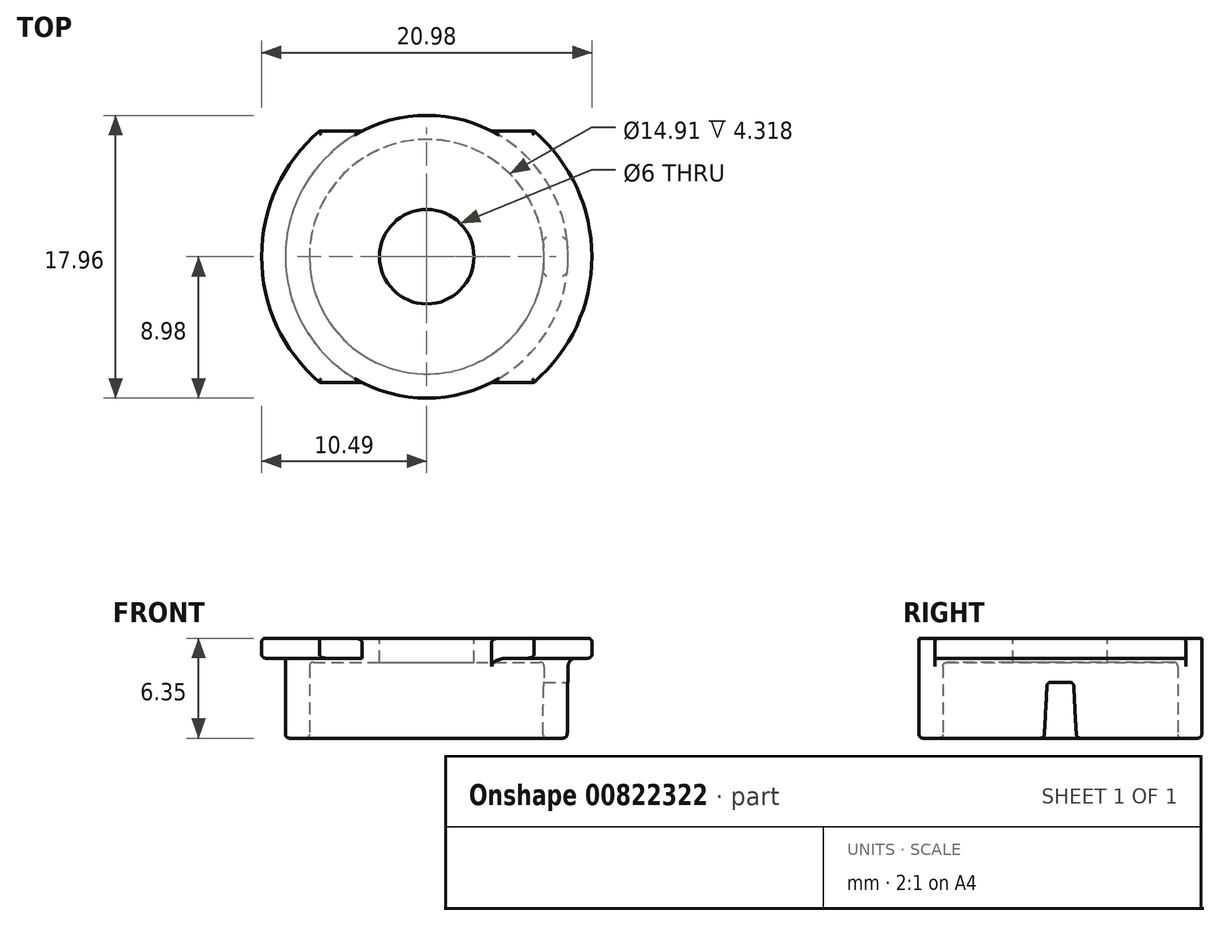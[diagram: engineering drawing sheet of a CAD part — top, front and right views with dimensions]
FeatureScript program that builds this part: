
annotation { "Feature Type Name" : "Feature", "Feature Type Description" : "" }
export const myFeature = defineFeature(function(context is Context, id is Id, definition is map)
    precondition{}
    {
        {
            var Q0;
            Q0=qCreatedBy(makeId("Top.planeOp"),FACE);
            var sketch = newSketch(context, id + "F0", { "sketchPlane" : qUnion([Q0])});
            skCircle(sketch, "E0", {"center": v(0, 0) * mm, "radius": 10.5 * mm});
            skLineSegment(sketch, "E1", {"start": v(-6.81, 7.98) * mm, "end": v(6.81, 7.98) * mm});
            skLineSegment(sketch, "E2", {"start": v(-6.81, -7.98) * mm, "end": v(6.81, -7.98) * mm});
            skSolve(sketch);
        }
        {
            var Q0;
            {var subQ0=sQuery(id+"F0.wireOp",EDGE,"E1");Q0=makeQuery(id+"F0.imprint","IMPRINT",FACE,{"disambiguationData":[TD([[makeQuery(id+"F0.imprint","IMPRINT",EDGE,{"derivedFrom":subQ0}),-1.0]])]});}
            extrude(context, id + "F1", {"entities" : qUnion([Q0]), "depth" : 1.27 * mm, "offsetDistance" : 25.4 * mm});
        }
        {
            var Q0;
            Q0=makeQuery(id+"F1.opExtrude","CAP_FACE",FACE,{"disambiguationData":[OSD([sQuery(id+"F0.wireOp",EDGE,"E0"),sQuery(id+"F0.wireOp",EDGE,"E1"),sQuery(id+"F0.wireOp",EDGE,"E2")])],"isStart":true});
            var sketch = newSketch(context, id + "F2", { "sketchPlane" : qUnion([Q0])});
            skCircle(sketch, "E3", {"center": v(0, 0) * mm, "radius": 8.98 * mm});
            skSolve(sketch);
        }
        {
            var Q0;
            Q0 = qSketchRegion(id + "F2", true);
            var Q1;
            Q1=makeQuery(id+"F1.opExtrude","CAP_FACE",FACE,{"disambiguationData":[OSD([sQuery(id+"F0.wireOp",EDGE,"E0"),sQuery(id+"F0.wireOp",EDGE,"E1"),sQuery(id+"F0.wireOp",EDGE,"E2")])],"isStart":false});
            extrude(context, id + "F3", {"entities" : qUnion([Q0]), "operationType" : NewBodyOperationType.ADD, "endBound" : BoundingType.UP_TO_SURFACE, "oppositeDirection" : true, "depth" : 5.08 * mm, "endBoundEntityFace" : qUnion([Q1]), "offsetDistance" : 25.4 * mm});
        }
        {
            var Q0;
            Q0=makeQuery(id+"F3.boolean.opBoolean","MERGE",FACE,{"derivedFrom":[makeQuery(id+"F1.opExtrude","CAP_FACE",FACE,{"disambiguationData":[OSD([sQuery(id+"F0.wireOp",EDGE,"E0"),sQuery(id+"F0.wireOp",EDGE,"E1"),sQuery(id+"F0.wireOp",EDGE,"E2")])],"isStart":true}),makeQuery(id+"F3.opExtrude","CAP_FACE",FACE,{"disambiguationData":[OSD([sQuery(id+"F2.wireOp",EDGE,"E3")])],"isStart":true})]});
            var sketch = newSketch(context, id + "F4", { "sketchPlane" : qUnion([Q0])});
            skCircle(sketch, "E4", {"center": v(0, 0) * mm, "radius": 8.98 * mm});
            skSolve(sketch);
        }
        {
            var Q0;
            Q0 = qSketchRegion(id + "F4", true);
            extrude(context, id + "F5", {"entities" : qUnion([Q0]), "operationType" : NewBodyOperationType.ADD, "depth" : 5.08 * mm, "offsetDistance" : 25.4 * mm});
        }
        {
            var Q0;
            Q0=makeQuery(id+"F5.opExtrude","CAP_FACE",FACE,{"disambiguationData":[OSD([sQuery(id+"F4.wireOp",EDGE,"E4")])],"isStart":false});
            var sketch = newSketch(context, id + "F6", { "sketchPlane" : qUnion([Q0])});
            skCircle(sketch, "E5", {"center": v(0, 0) * mm, "radius": 7.45 * mm});
            skSolve(sketch);
        }
        {
            var Q0;
            Q0 = qSketchRegion(id + "F6", true);
            extrude(context, id + "F7", {"entities" : qUnion([Q0]), "operationType" : NewBodyOperationType.REMOVE, "oppositeDirection" : true, "depth" : 4.83 * mm, "offsetDistance" : 25.4 * mm});
        }
        {
            var Q0;
            {var subQ0=sQuery(id+"F0.wireOp",EDGE,"E2");var subQ1=sQuery(id+"F0.wireOp",EDGE,"E1");var subQ2=sQuery(id+"F0.wireOp",EDGE,"E0");Q0=makeQuery(id+"F3.boolean.opBoolean","MERGE",FACE,{"derivedFrom":[makeQuery(id+"F1.opExtrude","CAP_FACE",FACE,{"disambiguationData":[OSD([subQ2,subQ1,subQ0])],"isStart":false}),makeQuery(id+"F3.opExtrude","CAP_FACE",FACE,{"disambiguationData":[OSD([subQ2,subQ1,subQ0])],"isStart":false})]});}
            var sketch = newSketch(context, id + "F8", { "sketchPlane" : qUnion([Q0])});
            skCircle(sketch, "E6", {"center": v(0, 0) * mm, "radius": 3 * mm});
            skSolve(sketch);
        }
        {
            var Q0;
            Q0 = qSketchRegion(id + "F8", true);
            extrude(context, id + "F9", {"entities" : qUnion([Q0]), "operationType" : NewBodyOperationType.REMOVE, "endBound" : BoundingType.UP_TO_NEXT, "oppositeDirection" : true, "depth" : 25.4 * mm, "offsetDistance" : 25.4 * mm});
        }
        {
            var Q0;
            Q0=qCreatedBy(makeId("Top.planeOp"),FACE);
            cPlane(context, id + "F10", {"entities" : qUnion([Q0]), "cplaneType" : CPlaneType.OFFSET, "offset" : 1.52 * mm, "oppositeDirection" : true, "width" : 152.4 * mm, "height" : 152.4 * mm});
        }
        {
            var Q0;
            Q0=qCreatedBy(id+"F10.planeOp",FACE);
            var sketch = newSketch(context, id + "F11", { "sketchPlane" : qUnion([Q0])});
            skLineSegment(sketch, "E7", {"start": v(8.94, 0.84) * mm, "end": v(7.4, 0.84) * mm});
            skLineSegment(sketch, "E8", {"start": v(8.94, -0.84) * mm, "end": v(7.4, -0.84) * mm});
            skArc(sketch, "E9", {"start": v(7.4, 0.84) * mm, "mid": v(7.45, 0) * mm, "end": v(7.4, -0.84) * mm});
            skArc(sketch, "E10", {"start": v(8.94, 0.84) * mm, "mid": v(8.98, 0) * mm, "end": v(8.94, -0.84) * mm});
            skSolve(sketch);
        }
        {
            var Q0;
            Q0 = qSketchRegion(id + "F11", true);
            extrude(context, id + "F12", {"entities" : qUnion([Q0]), "operationType" : NewBodyOperationType.REMOVE, "endBound" : BoundingType.UP_TO_NEXT, "oppositeDirection" : true, "depth" : 25.4 * mm, "offsetDistance" : 25.4 * mm, "hasDraft" : true, "draftAngle" : 3 * degree});
        }
        {
            var Q0;
            Q0=makeQuery(id+"F7.boolean.opBoolean","COPY",EDGE,{"derivedFrom":makeQuery(id+"F7.opExtrude","CAP_EDGE",EDGE,{"disambiguationData":[OSD([sQuery(id+"F6.wireOp",EDGE,"E5")])],"isStart":false})});
            fillet(context, id + "F13", {"entities" : qUnion([Q0]), "radius" : 0.25 * mm, "tangentPropagation" : true, "allowEdgeOverflow" : false});
        }
        {
            var Q0;
            Q0=makeQuery(id+"F12.boolean.opBoolean","COPY",EDGE,{"derivedFrom":makeQuery(id+"F12.opExtrude","CAP_EDGE",EDGE,{"disambiguationData":[OSD([sQuery(id+"F11.wireOp",EDGE,"E10")])],"isStart":true})});
            var Q1;
            Q1=makeQuery(id+"F12.boolean.opBoolean","COPY",EDGE,{"derivedFrom":makeQuery(id+"F12.opExtrude","CAP_EDGE",EDGE,{"disambiguationData":[OSD([sQuery(id+"F11.wireOp",EDGE,"E9")])],"isStart":true})});
            var Q2;
            Q2=makeQuery(id+"F12.boolean.opBoolean","COPY",EDGE,{"derivedFrom":makeQuery(id+"F12.opExtrude","CAP_EDGE",EDGE,{"disambiguationData":[OSD([sQuery(id+"F11.wireOp",EDGE,"E7")])],"isStart":true})});
            var Q3;
            Q3=makeQuery(id+"F12.boolean.opBoolean","COPY",EDGE,{"derivedFrom":makeQuery(id+"F12.opExtrude","CAP_EDGE",EDGE,{"disambiguationData":[OSD([sQuery(id+"F11.wireOp",EDGE,"E8")])],"isStart":true})});
            var Q4;
            Q4=makeQuery(id+"F12.boolean.opBoolean","COPY",EDGE,{"derivedFrom":makeQuery(id+"F12.opExtrude","TWEAK_EDGE",EDGE,{"derivedFrom":[makeQuery(id+"F5.opExtrude","CAP_FACE",FACE,{"disambiguationData":[OSD([sQuery(id+"F4.wireOp",EDGE,"E4")])],"isStart":false}),makeQuery(id+"F11.imprint","IMPRINT",EDGE,{"derivedFrom":sQuery(id+"F11.wireOp",EDGE,"E8")})]})});
            var Q5;
            Q5=makeQuery(id+"F12.boolean.opBoolean","COPY",EDGE,{"derivedFrom":makeQuery(id+"F12.opExtrude","TWEAK_EDGE",EDGE,{"derivedFrom":[makeQuery(id+"F5.opExtrude","CAP_FACE",FACE,{"disambiguationData":[OSD([sQuery(id+"F4.wireOp",EDGE,"E4")])],"isStart":false}),makeQuery(id+"F11.imprint","IMPRINT",EDGE,{"derivedFrom":sQuery(id+"F11.wireOp",EDGE,"E7")})]})});
            fillet(context, id + "F14", {"entities" : qUnion([Q0, Q1, Q2, Q3, Q4, Q5]), "radius" : 0.25 * mm, "tangentPropagation" : true, "allowEdgeOverflow" : false});
        }
        {
            var Q0;
            Q0=qCreatedBy(makeId("Front.planeOp"),FACE);
            var sketch = newSketch(context, id + "F15", { "sketchPlane" : qUnion([Q0])});
            skLineSegment(sketch, "E11", {"start": v(0, 0) * mm, "end": v(0, -25.4) * mm, "construction": true});
            skSolve(sketch);
        }
        {
            var Q0;
            {var subQ1=sQuery(id+"F4.wireOp",EDGE,"E4");Q0=makeQuery(id+"FYQlqfAHaxeDl4F_1.1.F12.boolean.opBoolean","SPLIT",FACE,{"disambiguationData":[TD([makeQuery(id+"FYQlqfAHaxeDl4F_1.1.F12.opExtrude","SWEPT_FACE",FACE,{"disambiguationData":[OSD([sQuery(id+"F11.wireOp",EDGE,"E7")])]})])],"derivedFrom":makeQuery(id+"F5.opExtrude","CAP_FACE",FACE,{"disambiguationData":[OSD([subQ1])],"isStart":false})});}
            var Q1;
            {var subQ0=sQuery(id+"F11.wireOp",EDGE,"E8");var subQ1=sQuery(id+"F4.wireOp",EDGE,"E4");var subQ4=sQuery(id+"F11.wireOp",EDGE,"E7");Q1=makeQuery(id+"FYQlqfAHaxeDl4F_1.3.F12.boolean.opBoolean","SPLIT",FACE,{"disambiguationData":[TD([makeQuery(id+"FYQlqfAHaxeDl4F_1.3.F12.opExtrude","SWEPT_FACE",FACE,{"disambiguationData":[OSD([subQ4])]})])],"derivedFrom":makeQuery(id+"FYQlqfAHaxeDl4F_1.2.F12.boolean.opBoolean","SPLIT",FACE,{"disambiguationData":[TD([makeQuery(id+"FYQlqfAHaxeDl4F_1.2.F12.opExtrude","SWEPT_FACE",FACE,{"disambiguationData":[OSD([subQ0])]})])],"derivedFrom":makeQuery(id+"FYQlqfAHaxeDl4F_1.1.F12.boolean.opBoolean","SPLIT",FACE,{"disambiguationData":[TD([makeQuery(id+"FYQlqfAHaxeDl4F_1.1.F12.opExtrude","SWEPT_FACE",FACE,{"disambiguationData":[OSD([subQ0])]})])],"derivedFrom":makeQuery(id+"F5.opExtrude","CAP_FACE",FACE,{"disambiguationData":[OSD([subQ1])],"isStart":false})})})});}
            var Q2;
            {var subQ1=sQuery(id+"F4.wireOp",EDGE,"E4");var subQ8=sQuery(id+"F11.wireOp",EDGE,"E8");Q2=makeQuery(id+"FYQlqfAHaxeDl4F_1.3.F12.boolean.opBoolean","SPLIT",FACE,{"disambiguationData":[TD([makeQuery(id+"FYQlqfAHaxeDl4F_1.3.F12.opExtrude","SWEPT_FACE",FACE,{"disambiguationData":[OSD([subQ8])]})])],"derivedFrom":makeQuery(id+"FYQlqfAHaxeDl4F_1.2.F12.boolean.opBoolean","SPLIT",FACE,{"disambiguationData":[TD([makeQuery(id+"FYQlqfAHaxeDl4F_1.2.F12.opExtrude","SWEPT_FACE",FACE,{"disambiguationData":[OSD([subQ8])]})])],"derivedFrom":makeQuery(id+"FYQlqfAHaxeDl4F_1.1.F12.boolean.opBoolean","SPLIT",FACE,{"disambiguationData":[TD([makeQuery(id+"FYQlqfAHaxeDl4F_1.1.F12.opExtrude","SWEPT_FACE",FACE,{"disambiguationData":[OSD([subQ8])]})])],"derivedFrom":makeQuery(id+"F5.opExtrude","CAP_FACE",FACE,{"disambiguationData":[OSD([subQ1])],"isStart":false})})})});}
            var Q3;
            {var subQ0=sQuery(id+"F11.wireOp",EDGE,"E8");var subQ1=sQuery(id+"F4.wireOp",EDGE,"E4");var subQ3=sQuery(id+"F11.wireOp",EDGE,"E7");Q3=makeQuery(id+"FYQlqfAHaxeDl4F_1.2.F12.boolean.opBoolean","SPLIT",FACE,{"disambiguationData":[TD([makeQuery(id+"FYQlqfAHaxeDl4F_1.2.F12.opExtrude","SWEPT_FACE",FACE,{"disambiguationData":[OSD([subQ3])]})])],"derivedFrom":makeQuery(id+"FYQlqfAHaxeDl4F_1.1.F12.boolean.opBoolean","SPLIT",FACE,{"disambiguationData":[TD([makeQuery(id+"FYQlqfAHaxeDl4F_1.1.F12.opExtrude","SWEPT_FACE",FACE,{"disambiguationData":[OSD([subQ0])]})])],"derivedFrom":makeQuery(id+"F5.opExtrude","CAP_FACE",FACE,{"disambiguationData":[OSD([subQ1])],"isStart":false})})});}
            fillet(context, id + "F16", {"entities" : qUnion([Q0, Q1, Q2, Q3]), "radius" : 0.25 * mm, "tangentPropagation" : true, "allowEdgeOverflow" : false});
        }
        {
            var Q0;
            Q0=makeQuery(id+"F5.boolean.opBoolean","SPLIT",EDGE,{"disambiguationData":[OD(1.0)],"derivedFrom":makeQuery(id+"F5.opExtrude","CAP_EDGE",EDGE,{"disambiguationData":[OSD([sQuery(id+"F4.wireOp",EDGE,"E4")])],"isStart":true})});
            var Q1;
            Q1=makeQuery(id+"F5.boolean.opBoolean","SPLIT",EDGE,{"disambiguationData":[OD(0.0)],"derivedFrom":makeQuery(id+"F5.opExtrude","CAP_EDGE",EDGE,{"disambiguationData":[OSD([sQuery(id+"F4.wireOp",EDGE,"E4")])],"isStart":true})});
            fillet(context, id + "F17", {"entities" : qUnion([Q0, Q1]), "radius" : 0.5 * mm, "tangentPropagation" : true, "allowEdgeOverflow" : false});
        }
        {
            var Q0;
            {var subQ1=sQuery(id+"F0.wireOp",EDGE,"E1");var subQ2=sQuery(id+"F0.wireOp",EDGE,"E0");Q0=makeQuery(id+"F3.boolean.opBoolean","SPLIT",EDGE,{"disambiguationData":[TD([makeQuery(id+"F1.opExtrude","SWEPT_FACE",FACE,{"disambiguationData":[OSD([subQ2]),TDD([makeQuery(id+"F0.imprint","IMPRINT",EDGE,{"disambiguationData":[TD([[makeQuery(id+"F0.imprint","INTERSECT",VERTEX,{"disambiguationData":[OD(0.0)],"derivedFrom":[subQ2,subQ1]}),-1.0]])],"derivedFrom":subQ2})])]})])],"derivedFrom":makeQuery(id+"F1.opExtrude","CAP_EDGE",EDGE,{"disambiguationData":[OSD([subQ1])],"isStart":false})});}
            var Q1;
            {var subQ0=sQuery(id+"F0.wireOp",EDGE,"E2");var subQ1=sQuery(id+"F0.wireOp",EDGE,"E1");var subQ2=sQuery(id+"F0.wireOp",EDGE,"E0");var subQ3=makeQuery(id+"F1.opExtrude","CAP_FACE",FACE,{"disambiguationData":[OSD([subQ2,subQ1,subQ0])],"isStart":false});var subQ4=sQuery(id+"F2.wireOp",EDGE,"E3");var subQ5=makeQuery(id+"F1.opExtrude","CAP_EDGE",EDGE,{"disambiguationData":[OSD([subQ0])],"isStart":true});var subQ6=makeQuery(id+"F2.imprint","INTERSECT",VERTEX,{"disambiguationData":[OD(1.0)],"derivedFrom":[subQ5,subQ4]});var subQ7=makeQuery(id+"F1.opExtrude","CAP_EDGE",EDGE,{"disambiguationData":[OSD([subQ1])],"isStart":true});var subQ9=makeQuery(id+"F2.imprint","INTERSECT",VERTEX,{"disambiguationData":[OD(0.0)],"derivedFrom":[subQ7,subQ4]});var subQ10=makeQuery(id+"F2.imprint","INTERSECT",VERTEX,{"disambiguationData":[OD(0.0)],"derivedFrom":[subQ5,subQ4]});Q1=makeQuery(id+"F3.boolean.opBoolean","SPLIT",EDGE,{"disambiguationData":[TD([makeQuery(id+"F1.opExtrude","SWEPT_FACE",FACE,{"disambiguationData":[OSD([subQ1])]})])],"derivedFrom":makeQuery(id+"F3.opExtrude","TWEAK_EDGE",EDGE,{"derivedFrom":[subQ3,makeQuery(id+"F2.imprint","IMPRINT",EDGE,{"disambiguationData":[TD([[subQ10,1.0]])],"derivedFrom":subQ4}),makeQuery(id+"F2.imprint","IMPRINT",EDGE,{"disambiguationData":[TD([[subQ10,-1.0]])],"derivedFrom":subQ4}),makeQuery(id+"F2.imprint","IMPRINT",EDGE,{"disambiguationData":[TD([[subQ9,-1.0]])],"derivedFrom":subQ4}),makeQuery(id+"F2.imprint","IMPRINT",EDGE,{"disambiguationData":[TD([[subQ6,1.0]])],"derivedFrom":subQ4})]})});}
            var Q2;
            {var subQ0=sQuery(id+"F0.wireOp",EDGE,"E1");var subQ2=sQuery(id+"F0.wireOp",EDGE,"E0");Q2=makeQuery(id+"F3.boolean.opBoolean","SPLIT",EDGE,{"disambiguationData":[TD([makeQuery(id+"F1.opExtrude","SWEPT_FACE",FACE,{"disambiguationData":[OSD([subQ2]),TDD([makeQuery(id+"F0.imprint","IMPRINT",EDGE,{"disambiguationData":[TD([[makeQuery(id+"F0.imprint","INTERSECT",VERTEX,{"disambiguationData":[OD(1.0)],"derivedFrom":[subQ2,subQ0]}),1.0]])],"derivedFrom":subQ2})])]})])],"derivedFrom":makeQuery(id+"F1.opExtrude","CAP_EDGE",EDGE,{"disambiguationData":[OSD([subQ0])],"isStart":false})});}
            var Q3;
            {var subQ0=sQuery(id+"F0.wireOp",EDGE,"E0");Q3=makeQuery(id+"F1.opExtrude","CAP_EDGE",EDGE,{"disambiguationData":[OSD([subQ0]),TDD([makeQuery(id+"F0.imprint","IMPRINT",EDGE,{"disambiguationData":[TD([[makeQuery(id+"F0.imprint","INTERSECT",VERTEX,{"disambiguationData":[OD(1.0)],"derivedFrom":[subQ0,sQuery(id+"F0.wireOp",EDGE,"E1")]}),1.0]])],"derivedFrom":subQ0})])],"isStart":false});}
            var Q4;
            {var subQ0=sQuery(id+"F0.wireOp",EDGE,"E2");var subQ1=sQuery(id+"F0.wireOp",EDGE,"E1");var subQ2=sQuery(id+"F0.wireOp",EDGE,"E0");Q4=makeQuery(id+"F3.boolean.opBoolean","SPLIT",EDGE,{"disambiguationData":[TD([makeQuery(id+"F1.opExtrude","SWEPT_FACE",FACE,{"disambiguationData":[OSD([subQ2]),TDD([makeQuery(id+"F0.imprint","IMPRINT",EDGE,{"disambiguationData":[TD([[makeQuery(id+"F0.imprint","INTERSECT",VERTEX,{"disambiguationData":[OD(1.0)],"derivedFrom":[subQ2,subQ1]}),1.0]])],"derivedFrom":subQ2})])]})])],"derivedFrom":makeQuery(id+"F1.opExtrude","CAP_EDGE",EDGE,{"disambiguationData":[OSD([subQ0])],"isStart":false})});}
            var Q5;
            {var subQ0=sQuery(id+"F0.wireOp",EDGE,"E2");var subQ1=sQuery(id+"F0.wireOp",EDGE,"E1");var subQ2=sQuery(id+"F0.wireOp",EDGE,"E0");var subQ3=makeQuery(id+"F1.opExtrude","CAP_FACE",FACE,{"disambiguationData":[OSD([subQ2,subQ1,subQ0])],"isStart":false});var subQ4=sQuery(id+"F2.wireOp",EDGE,"E3");var subQ5=makeQuery(id+"F1.opExtrude","CAP_EDGE",EDGE,{"disambiguationData":[OSD([subQ0])],"isStart":true});var subQ6=makeQuery(id+"F2.imprint","INTERSECT",VERTEX,{"disambiguationData":[OD(1.0)],"derivedFrom":[subQ5,subQ4]});var subQ7=makeQuery(id+"F1.opExtrude","CAP_EDGE",EDGE,{"disambiguationData":[OSD([subQ1])],"isStart":true});var subQ9=makeQuery(id+"F2.imprint","INTERSECT",VERTEX,{"disambiguationData":[OD(0.0)],"derivedFrom":[subQ7,subQ4]});var subQ10=makeQuery(id+"F2.imprint","INTERSECT",VERTEX,{"disambiguationData":[OD(0.0)],"derivedFrom":[subQ5,subQ4]});Q5=makeQuery(id+"F3.boolean.opBoolean","SPLIT",EDGE,{"disambiguationData":[TD([makeQuery(id+"F1.opExtrude","SWEPT_FACE",FACE,{"disambiguationData":[OSD([subQ0])]})])],"derivedFrom":makeQuery(id+"F3.opExtrude","TWEAK_EDGE",EDGE,{"derivedFrom":[subQ3,makeQuery(id+"F2.imprint","IMPRINT",EDGE,{"disambiguationData":[TD([[subQ10,1.0]])],"derivedFrom":subQ4}),makeQuery(id+"F2.imprint","IMPRINT",EDGE,{"disambiguationData":[TD([[subQ10,-1.0]])],"derivedFrom":subQ4}),makeQuery(id+"F2.imprint","IMPRINT",EDGE,{"disambiguationData":[TD([[subQ9,-1.0]])],"derivedFrom":subQ4}),makeQuery(id+"F2.imprint","IMPRINT",EDGE,{"disambiguationData":[TD([[subQ6,1.0]])],"derivedFrom":subQ4})]})});}
            var Q6;
            {var subQ0=sQuery(id+"F0.wireOp",EDGE,"E2");var subQ1=sQuery(id+"F0.wireOp",EDGE,"E1");var subQ2=sQuery(id+"F0.wireOp",EDGE,"E0");Q6=makeQuery(id+"F3.boolean.opBoolean","SPLIT",EDGE,{"disambiguationData":[TD([makeQuery(id+"F1.opExtrude","SWEPT_FACE",FACE,{"disambiguationData":[OSD([subQ2]),TDD([makeQuery(id+"F0.imprint","IMPRINT",EDGE,{"disambiguationData":[TD([[makeQuery(id+"F0.imprint","INTERSECT",VERTEX,{"disambiguationData":[OD(0.0)],"derivedFrom":[subQ2,subQ1]}),-1.0]])],"derivedFrom":subQ2})])]})])],"derivedFrom":makeQuery(id+"F1.opExtrude","CAP_EDGE",EDGE,{"disambiguationData":[OSD([subQ0])],"isStart":false})});}
            var Q7;
            {var subQ0=sQuery(id+"F0.wireOp",EDGE,"E0");Q7=makeQuery(id+"F1.opExtrude","CAP_EDGE",EDGE,{"disambiguationData":[OSD([subQ0]),TDD([makeQuery(id+"F0.imprint","IMPRINT",EDGE,{"disambiguationData":[TD([[makeQuery(id+"F0.imprint","INTERSECT",VERTEX,{"disambiguationData":[OD(0.0)],"derivedFrom":[subQ0,sQuery(id+"F0.wireOp",EDGE,"E1")]}),-1.0]])],"derivedFrom":subQ0})])],"isStart":false});}
            var Q8;
            {var subQ0=sQuery(id+"F0.wireOp",EDGE,"E0");Q8=makeQuery(id+"F1.opExtrude","CAP_EDGE",EDGE,{"disambiguationData":[OSD([subQ0]),TDD([makeQuery(id+"F0.imprint","IMPRINT",EDGE,{"disambiguationData":[TD([[makeQuery(id+"F0.imprint","INTERSECT",VERTEX,{"disambiguationData":[OD(1.0)],"derivedFrom":[subQ0,sQuery(id+"F0.wireOp",EDGE,"E1")]}),1.0]])],"derivedFrom":subQ0})])],"isStart":true});}
            var Q9;
            {var subQ0=sQuery(id+"F0.wireOp",EDGE,"E0");Q9=makeQuery(id+"F1.opExtrude","CAP_EDGE",EDGE,{"disambiguationData":[OSD([subQ0]),TDD([makeQuery(id+"F0.imprint","IMPRINT",EDGE,{"disambiguationData":[TD([[makeQuery(id+"F0.imprint","INTERSECT",VERTEX,{"disambiguationData":[OD(0.0)],"derivedFrom":[subQ0,sQuery(id+"F0.wireOp",EDGE,"E1")]}),-1.0]])],"derivedFrom":subQ0})])],"isStart":true});}
            fillet(context, id + "F18", {"entities" : qUnion([Q0, Q1, Q2, Q3, Q4, Q5, Q6, Q7, Q8, Q9]), "radius" : 0.25 * mm, "tangentPropagation" : true, "allowEdgeOverflow" : false});
        }
    });
